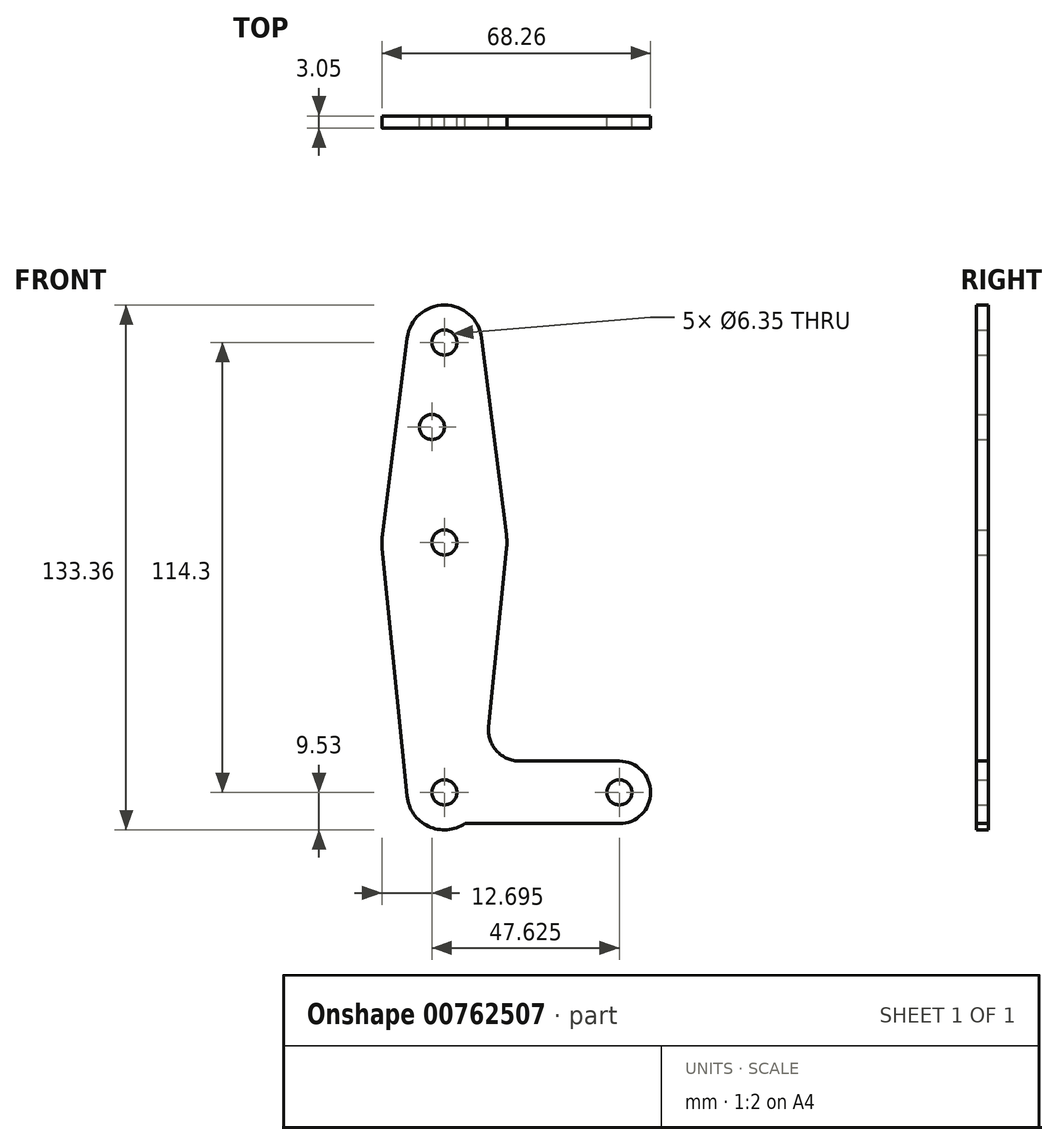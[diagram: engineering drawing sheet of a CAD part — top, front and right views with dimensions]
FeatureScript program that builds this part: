
annotation { "Feature Type Name" : "Feature", "Feature Type Description" : "" }
export const myFeature = defineFeature(function(context is Context, id is Id, definition is map)
    precondition{}
    {
        {
            var Q0;
            Q0=qCreatedBy(makeId("Front.planeOp"),FACE);
            var sketch = newSketch(context, id + "F0", { "sketchPlane" : qUnion([Q0])});
            skLineSegment(sketch, "E0", {"start": v(0, -5.97) * mm, "end": v(0, 114.3) * mm, "construction": true});
            skLineSegment(sketch, "E1", {"start": v(0, 0) * mm, "end": v(44.45, 0) * mm, "construction": true});
            skCircle(sketch, "E2", {"center": v(0, 114.3) * mm, "radius": 9.53 * mm});
            skCircle(sketch, "E3", {"center": v(0, 0) * mm, "radius": 9.53 * mm});
            skCircle(sketch, "E4", {"center": v(44.45, 0) * mm, "radius": 7.94 * mm});
            skCircle(sketch, "E5", {"center": v(0, 63.5) * mm, "radius": 15.88 * mm});
            skLineSegment(sketch, "E6", {"start": v(-9.45, 115.5) * mm, "end": v(-15.75, 65.48) * mm});
            skLineSegment(sketch, "E7", {"start": v(9.45, 115.5) * mm, "end": v(15.75, 65.48) * mm});
            skLineSegment(sketch, "E8", {"start": v(15.8, 61.91) * mm, "end": v(11.25, 16.68) * mm});
            skLineSegment(sketch, "E9", {"start": v(-15.8, 61.91) * mm, "end": v(-9.48, -0.95) * mm});
            skLineSegment(sketch, "E10", {"start": v(19.16, 7.94) * mm, "end": v(44.45, 7.94) * mm});
            skLineSegment(sketch, "E11", {"start": v(5.27, -7.94) * mm, "end": v(44.45, -7.94) * mm});
            skCircle(sketch, "E12", {"center": v(0, 114.3) * mm, "radius": 3.18 * mm});
            skCircle(sketch, "E13", {"center": v(-3.18, 92.85) * mm, "radius": 3.18 * mm});
            skCircle(sketch, "E14", {"center": v(0, 63.5) * mm, "radius": 3.18 * mm});
            skCircle(sketch, "E15", {"center": v(0, 0) * mm, "radius": 3.18 * mm});
            skCircle(sketch, "E16", {"center": v(44.45, 0) * mm, "radius": 3.18 * mm});
            skArc(sketch, "E17.filletArc", {"start": v(11.25, 16.68) * mm, "mid": v(13.26, 10.55) * mm, "end": v(19.16, 7.94) * mm});
            skSolve(sketch);
        }
        {
            var Q0;
            Q0 = qSketchRegion(id + "F0", true);
            extrude(context, id + "F1", {"entities" : qUnion([Q0]), "depth" : 3.05 * mm, "offsetDistance" : 25.4 * mm});
        }
    });
